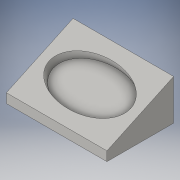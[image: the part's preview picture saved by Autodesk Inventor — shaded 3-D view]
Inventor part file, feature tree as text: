
AUTODESK INVENTOR PART (.ipt)
format: ipt  version: 2016 (Build 200138000, 138)  size: 108,032 bytes
history: native  units: in
note: dims shown in document units (in); Inventor stores cm internally (conversion verified against a paired STEP export)
features: extrude x2, sketch x2
ambient origin geometry x8: Origin, YZ Plane, XZ Plane, XY Plane, X Axis, Y Axis, Z Axis, Center Point
bodies: Solid1 (feature_tree)
feature tree (4):
  extrude  "Extrusion1"  TaperAngle=0.0deg  [1 undecoded]
  extrude  "Extrusion3"  [1 undecoded]
  sketch  "Sketch1"  dims[d4=0.0in d12=0.0in]
  sketch  "Sketch5"
note: 2 required parameter values undecoded (feature->parameter linkage not recoverable at this tier; creation-order binding heuristic only, values carry confidence <= 0.55)
